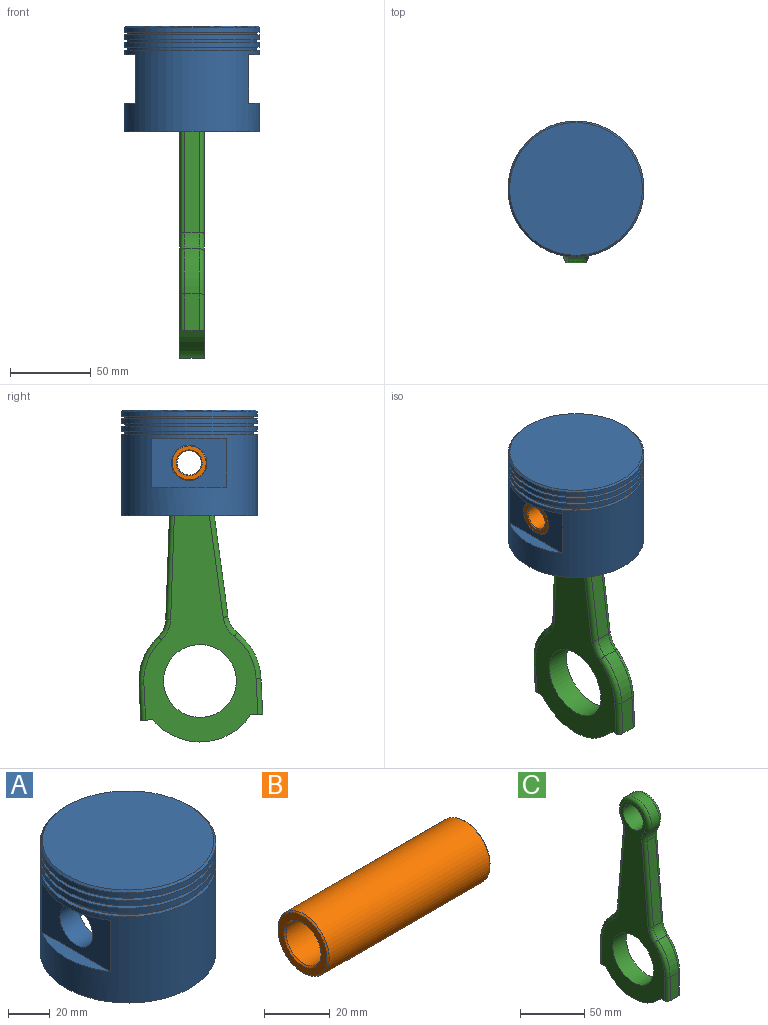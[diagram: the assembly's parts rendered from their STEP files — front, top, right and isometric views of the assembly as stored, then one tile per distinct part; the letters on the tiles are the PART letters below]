
ASSEMBLY  parts=3 mates=2
PART A: 29 faces, bbox 84x84x65.4 mm
  f0: cylinder r=42mm len=84mm, axis (0,0,-1), area 10348.4mm2, adj f14,f16,f23,f24,f25,f26,f27,f28
  f1: cylinder r=11mm len=22mm, axis (1,0,0), area 863.9mm2, adj f19,f25
  f2: cylinder r=42mm len=84mm, axis (0,0,-1), area 791.7mm2, adj f4,f5
  f3: plane 82x82mm, normal (0,0,1), area 5281mm2, adj f4
  f4: cone r=41mm half-angle=45deg, axis (0,0,-1), area 368.8mm2, adj f2,f3
  f5: plane 84x84mm, normal (0,0,-1), area 515.2mm2, adj f2,f7
  f6: plane 84x84mm, normal (0,0,1), area 515.2mm2, adj f7,f8
  f7: cylinder r=40mm len=80mm, axis (0,0,1), area 377mm2, adj f5,f6
  f8: cylinder r=42mm len=84mm, axis (0,0,-1), area 791.7mm2, adj f6,f9
  f9: plane 84x84mm, normal (0,0,-1), area 515.2mm2, adj f8,f11
  f10: plane 84x84mm, normal (0,0,1), area 515.2mm2, adj f11,f12
  f11: cylinder r=40mm len=80mm, axis (0,0,1), area 377mm2, adj f9,f10
  f12: cylinder r=42mm len=84mm, axis (0,0,-1), area 791.7mm2, adj f10,f13
  f13: plane 84x84mm, normal (0,0,-1), area 515.2mm2, adj f12,f15
  f14: plane 84x84mm, normal (0,0,1), area 515.2mm2, adj f0,f15
  f15: cylinder r=40mm len=80mm, axis (0,0,1), area 502.7mm2, adj f13,f14
  f16: plane 84x84mm, normal (0,0,-1), area 2333.7mm2, adj f0,f18,f19,f20,f21
  f17: plane 76x45mm, normal (0,0,-1), area 3208.1mm2, adj f18,f19,f20,f21
  f18: cylinder r=38mm len=60.4mm, axis (0,0,-1), area 2908.8mm2, adj f16,f17,f19,f20
  f19: plane 61.25x60.4mm, normal (1,0,0), area 3319.1mm2, adj f1,f16,f17,f18,f21
  f20: plane 61.25x60.4mm, normal (-1,0,0), area 3319.1mm2, adj f16,f17,f18,f21,f22
  f21: cylinder r=38mm len=60.4mm, axis (0,0,-1), area 2908.8mm2, adj f16,f17,f19,f20
  f22: cylinder r=11mm len=22mm, axis (1,0,0), area 863.9mm2, adj f20,f28
  f23: plane 46.43x7mm, normal (0,0,-1), area 220.6mm2, adj f0,f25
  f24: plane 46.43x7mm, normal (0,0,1), area 220.6mm2, adj f0,f25
  f25: plane 46.43x30mm, normal (-1,0,0), area 1012.8mm2, adj f0,f1,f23,f24
  f26: plane 46.43x7mm, normal (0,0,-1), area 220.6mm2, adj f0,f28
  f27: plane 46.43x7mm, normal (0,0,1), area 220.6mm2, adj f0,f28
  f28: plane 46.43x30mm, normal (1,0,0), area 1012.8mm2, adj f0,f22,f26,f27
PART B: 8 faces, bbox 70x22x22 mm
  f0: cylinder r=7.5mm len=69mm, axis (-1,0,0), area 3251.5mm2, adj f4,f6
  f1: cylinder r=11mm len=69mm, axis (-1,0,0), area 4768.9mm2, adj f5,f7
  f2: plane 21x21mm, normal (1,0,0), area 145.3mm2, adj f6,f7
  f3: plane 21x21mm, normal (-1,0,0), area 145.3mm2, adj f4,f5
  f4: cone r=8mm half-angle=45deg, axis (-1,0,0), area 34.4mm2, adj f0,f3
  f5: cone r=11mm half-angle=45deg, axis (1,0,0), area 47.8mm2, adj f1,f3
  f6: cone r=7.5mm half-angle=45deg, axis (1,0,0), area 34.4mm2, adj f0,f2
  f7: cone r=10.5mm half-angle=45deg, axis (-1,0,0), area 47.8mm2, adj f1,f2
PART C: 40 faces, bbox 15x81.7x191.1 mm
  f0: cylinder r=37.72mm len=28.71mm, axis (-1,0,0), area 293.6mm2, adj f1,f17,f19,f30
  f1: plane 22.5x9mm, normal (0,-1,0), area 202.5mm2, adj f0,f2,f18,f29
  f2: plane 15x7.45mm, normal (0,0,-1), area 107.8mm2, adj f1,f3,f12,f13,f18,f29
  f3: cylinder r=37.72mm len=60.56mm, axis (-1,0,0), area 1054.4mm2, adj f2,f4,f12,f13
  f4: plane 15x7.45mm, normal (0,0,-1), area 107.8mm2, adj f3,f5,f12,f13,f28,f39
  f5: plane 22.5x9mm, normal (0,1,0), area 202.5mm2, adj f4,f6,f28,f39
  f6: cylinder r=37.72mm len=28.71mm, axis (-1,0,0), area 293.6mm2, adj f5,f14,f27,f38
  f7: plane 78.51x9mm, normal (0,1,0.09), area 709.2mm2, adj f14,f15,f25,f36
  f8: cylinder r=17mm len=34mm, axis (-1,0,0), area 645mm2, adj f15,f16,f23,f34
  f9: cylinder r=22.5mm len=45mm, axis (-1,0,0), area 2120.6mm2, adj f12,f13
  f10: cylinder r=11mm len=22mm, axis (-1,0,0), area 1036.7mm2, adj f12,f13
  f11: plane 78.51x9mm, normal (0,-1,0.09), area 709.2mm2, adj f16,f17,f21,f32
  f12: plane 186.72x69.45mm, normal (1,0,0), area 5068mm2, adj f2,f3,f4,f9,f10,f29,f30,f31
  f13: plane 186.72x69.45mm, normal (-1,0,0), area 5068mm2, adj f2,f3,f4,f9,f10,f18,f19,f20
  f14: cylinder r=15mm len=10.14mm, axis (-1,0,0), area 105.2mm2, adj f6,f7,f26,f37
  f15: cylinder r=15mm len=9mm, axis (-1,0,0), area 84mm2, adj f7,f8,f24,f35
  f16: cylinder r=15mm len=9mm, axis (-1,0,0), area 84mm2, adj f8,f11,f22,f33
  f17: cylinder r=15mm len=10.14mm, axis (-1,0,0), area 105.2mm2, adj f0,f11,f20,f31
  f18: cylinder r=3mm len=22.5mm, axis (0,0,-1), area 106mm2, adj f1,f2,f13,f19
  f19: torus R=34.72mm, axis (1,0,0), area 149.3mm2, adj f0,f13,f18,f20
  f20: torus R=18mm, axis (1,0,0), area 59.1mm2, adj f13,f17,f19,f21
  f21: cylinder r=3mm len=78.76mm, axis (0,-0.09,-1), area 371.3mm2, adj f11,f13,f20,f22
  f22: torus R=18mm, axis (1,0,0), area 47.2mm2, adj f13,f16,f21,f23
  f23: torus R=14mm, axis (1,0,0), area 316.1mm2, adj f8,f13,f22,f24
  f24: torus R=18mm, axis (1,0,0), area 47.2mm2, adj f13,f15,f23,f25
  f25: cylinder r=3mm len=78.76mm, axis (0,-0.09,1), area 371.3mm2, adj f7,f13,f24,f26
  f26: torus R=18mm, axis (1,0,0), area 59.1mm2, adj f13,f14,f25,f27
  f27: torus R=34.72mm, axis (1,0,0), area 149.3mm2, adj f6,f13,f26,f28
  f28: cylinder r=3mm len=22.5mm, axis (0,0,1), area 106mm2, adj f4,f5,f13,f27
  f29: cylinder r=3mm len=22.5mm, axis (0,0,1), area 106mm2, adj f1,f2,f12,f30
  f30: torus R=34.72mm, axis (1,0,0), area 149.3mm2, adj f0,f12,f29,f31
  f31: torus R=18mm, axis (1,0,0), area 59.1mm2, adj f12,f17,f30,f32
  f32: cylinder r=3mm len=78.76mm, axis (0,0.09,1), area 371.3mm2, adj f11,f12,f31,f33
  f33: torus R=18mm, axis (1,0,0), area 47.2mm2, adj f12,f16,f32,f34
  f34: torus R=14mm, axis (1,0,0), area 316.1mm2, adj f8,f12,f33,f35
  f35: torus R=18mm, axis (1,0,0), area 47.2mm2, adj f12,f15,f34,f36
  f36: cylinder r=3mm len=78.76mm, axis (0,0.09,-1), area 371.3mm2, adj f7,f12,f35,f37
  f37: torus R=18mm, axis (1,0,0), area 59.1mm2, adj f12,f14,f36,f38
  f38: torus R=34.72mm, axis (1,0,0), area 149.3mm2, adj f6,f12,f37,f39
  f39: cylinder r=3mm len=22.5mm, axis (0,0,-1), area 106mm2, adj f4,f5,f12,f38
PLACE A at identity fixed
PLACE B at identity
PLACE C rot(axis=(-1,0,0),2.8deg) t=(0,-6.69,-134.83)mm
MATE revolute C.f10 <-> B.f1  axis (-1,0,0) through (0,0,0)mm
MATE fastened B.f1 <-> A.f1  axis (1,0,0) through (35,0,0)mm
